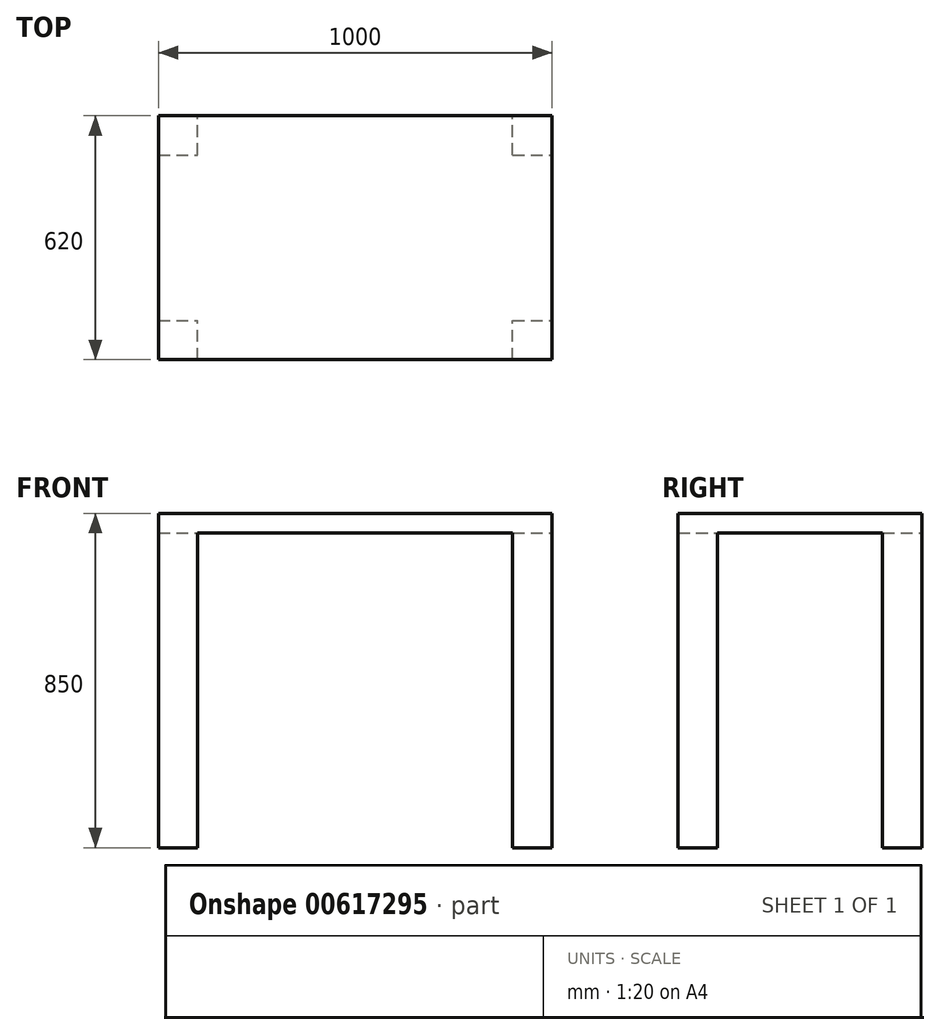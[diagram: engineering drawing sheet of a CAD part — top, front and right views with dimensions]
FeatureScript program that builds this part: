
annotation { "Feature Type Name" : "Feature", "Feature Type Description" : "" }
export const myFeature = defineFeature(function(context is Context, id is Id, definition is map)
    precondition{}
    {
        {
            var Q0;
            Q0=qCreatedBy(makeId("Top.planeOp"),FACE);
            var sketch = newSketch(context, id + "F0", { "sketchPlane" : qUnion([Q0])});
            skLineSegment(sketch, "E0.bottom", {"start": v(-44.43, 587.99) * mm, "end": v(955.57, 587.99) * mm});
            skLineSegment(sketch, "E0.top", {"start": v(-44.43, -32.01) * mm, "end": v(955.57, -32.01) * mm});
            skLineSegment(sketch, "E0.left", {"start": v(-44.43, 587.99) * mm, "end": v(-44.43, -32.01) * mm});
            skLineSegment(sketch, "E0.right", {"start": v(955.57, 587.99) * mm, "end": v(955.57, -32.01) * mm});
            skSolve(sketch);
        }
        {
            var Q0;
            Q0=makeQuery(id+"F0.imprint","IMPRINT",FACE,{"disambiguationData":[TD([[makeQuery(id+"F0.imprint","IMPRINT",EDGE,{"derivedFrom":sQuery(id+"F0.wireOp",EDGE,"E0.bottom")}),-1.0]])]});
            extrude(context, id + "F1", {"entities" : qUnion([Q0]), "depth" : 850 * mm, "offsetDistance" : 25 * mm});
        }
        {
            var Q0;
            Q0=qCreatedBy(makeId("Top.planeOp"),FACE);
            var sketch = newSketch(context, id + "F2", { "sketchPlane" : qUnion([Q0])});
            skLineSegment(sketch, "E1.bottom", {"start": v(-44.43, 67.99) * mm, "end": v(955.57, 67.99) * mm});
            skLineSegment(sketch, "E1.top", {"start": v(-44.43, 487.99) * mm, "end": v(955.57, 487.99) * mm});
            skLineSegment(sketch, "E1.left", {"start": v(-44.43, 67.99) * mm, "end": v(-44.43, 487.99) * mm});
            skLineSegment(sketch, "E1.right", {"start": v(955.57, 67.99) * mm, "end": v(955.57, 487.99) * mm});
            skSolve(sketch);
        }
        {
            var Q0;
            Q0 = qSketchRegion(id + "F2", true);
            extrude(context, id + "F3", {"entities" : qUnion([Q0]), "operationType" : NewBodyOperationType.REMOVE, "depth" : 800 * mm, "offsetDistance" : 25 * mm});
        }
        {
            var Q0;
            Q0=qCreatedBy(makeId("Top.planeOp"),FACE);
            var sketch = newSketch(context, id + "F4", { "sketchPlane" : qUnion([Q0])});
            skLineSegment(sketch, "E2.bottom", {"start": v(855.57, -32.01) * mm, "end": v(55.57, -32.01) * mm});
            skLineSegment(sketch, "E2.top", {"start": v(855.57, 587.99) * mm, "end": v(55.57, 587.99) * mm});
            skLineSegment(sketch, "E2.left", {"start": v(855.57, -32.01) * mm, "end": v(855.57, 587.99) * mm});
            skLineSegment(sketch, "E2.right", {"start": v(55.57, -32.01) * mm, "end": v(55.57, 587.99) * mm});
            skSolve(sketch);
        }
        {
            var Q0;
            Q0 = qSketchRegion(id + "F4", true);
            extrude(context, id + "F5", {"entities" : qUnion([Q0]), "operationType" : NewBodyOperationType.REMOVE, "depth" : 800 * mm, "offsetDistance" : 25 * mm});
        }
    });
